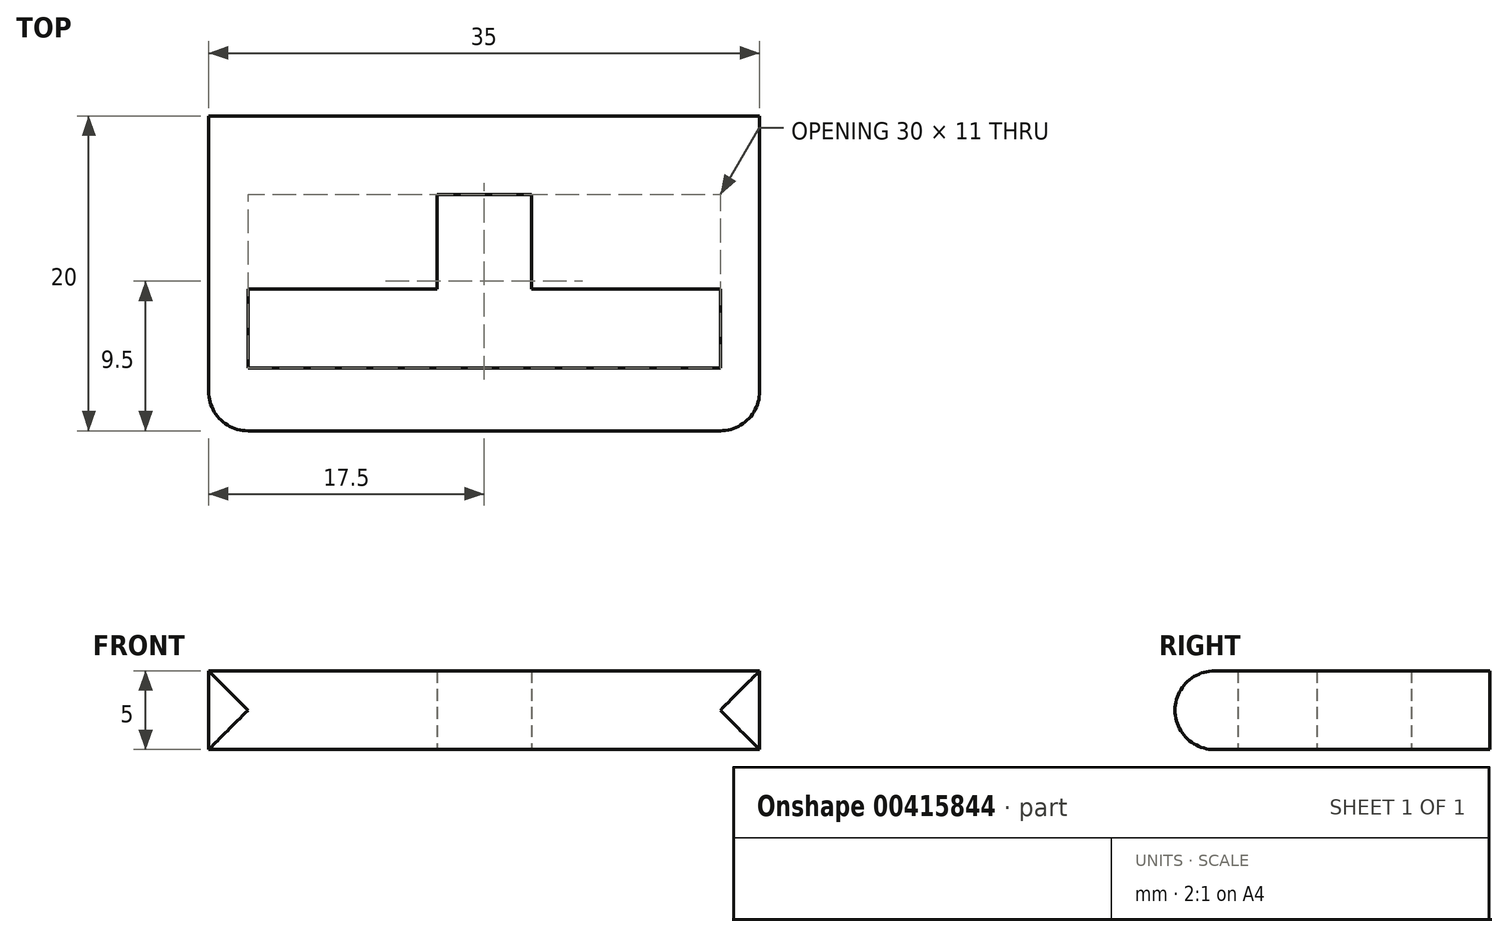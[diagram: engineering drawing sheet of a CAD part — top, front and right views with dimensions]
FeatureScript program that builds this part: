
annotation { "Feature Type Name" : "Feature", "Feature Type Description" : "" }
export const myFeature = defineFeature(function(context is Context, id is Id, definition is map)
    precondition{}
    {
        {
            var Q0;
            Q0=qCreatedBy(makeId("Top.planeOp"),FACE);
            var sketch = newSketch(context, id + "F0", { "sketchPlane" : qUnion([Q0])});
            skLineSegment(sketch, "E0.bottom", {"start": v(17.5, 10) * mm, "end": v(-17.5, 10) * mm});
            skLineSegment(sketch, "E0.top", {"start": v(17.5, -10) * mm, "end": v(-17.5, -10) * mm});
            skLineSegment(sketch, "E0.left", {"start": v(17.5, 10) * mm, "end": v(17.5, -10) * mm});
            skLineSegment(sketch, "E0.right", {"start": v(-17.5, 10) * mm, "end": v(-17.5, -10) * mm});
            skPoint(sketch, "E0.middle", {"position": v(0, 0) * mm});
            skLineSegment(sketch, "E1.bottom", {"start": v(15, -1) * mm, "end": v(-15, -1) * mm});
            skLineSegment(sketch, "E1.top", {"start": v(15, -6) * mm, "end": v(-15, -6) * mm});
            skLineSegment(sketch, "E1.left", {"start": v(15, -1) * mm, "end": v(15, -6) * mm});
            skLineSegment(sketch, "E1.right", {"start": v(-15, -1) * mm, "end": v(-15, -6) * mm});
            skPoint(sketch, "E1.middle", {"position": v(0, -3.5) * mm});
            skLineSegment(sketch, "E2.bottom", {"start": v(3, 5) * mm, "end": v(-3, 5) * mm});
            skLineSegment(sketch, "E2.top", {"start": v(3, -1) * mm, "end": v(-3, -1) * mm});
            skLineSegment(sketch, "E2.left", {"start": v(3, 5) * mm, "end": v(3, -1) * mm});
            skLineSegment(sketch, "E2.right", {"start": v(-3, 5) * mm, "end": v(-3, -1) * mm});
            skPoint(sketch, "E2.middle", {"position": v(0, 2) * mm});
            skSolve(sketch);
        }
        {
            var Q0;
            Q0=makeQuery(id+"F0.imprint","IMPRINT",FACE,{"disambiguationData":[TD([[makeQuery(id+"F0.imprint","IMPRINT",EDGE,{"derivedFrom":sQuery(id+"F0.wireOp",EDGE,"E0.bottom")}),1.0]])]});
            extrude(context, id + "F1", {"entities" : qUnion([Q0]), "depth" : 5 * mm});
        }
        {
            var Q0;
            Q0=makeQuery(id+"F1.opExtrude","SWEPT_FACE",FACE,{"disambiguationData":[OSD([sQuery(id+"F0.wireOp",EDGE,"E0.top")])]});
            fillet(context, id + "F2", {"entities" : qUnion([Q0]), "radius" : 2.5 * mm, "tangentPropagation" : true, "allowEdgeOverflow" : false});
        }
    });
